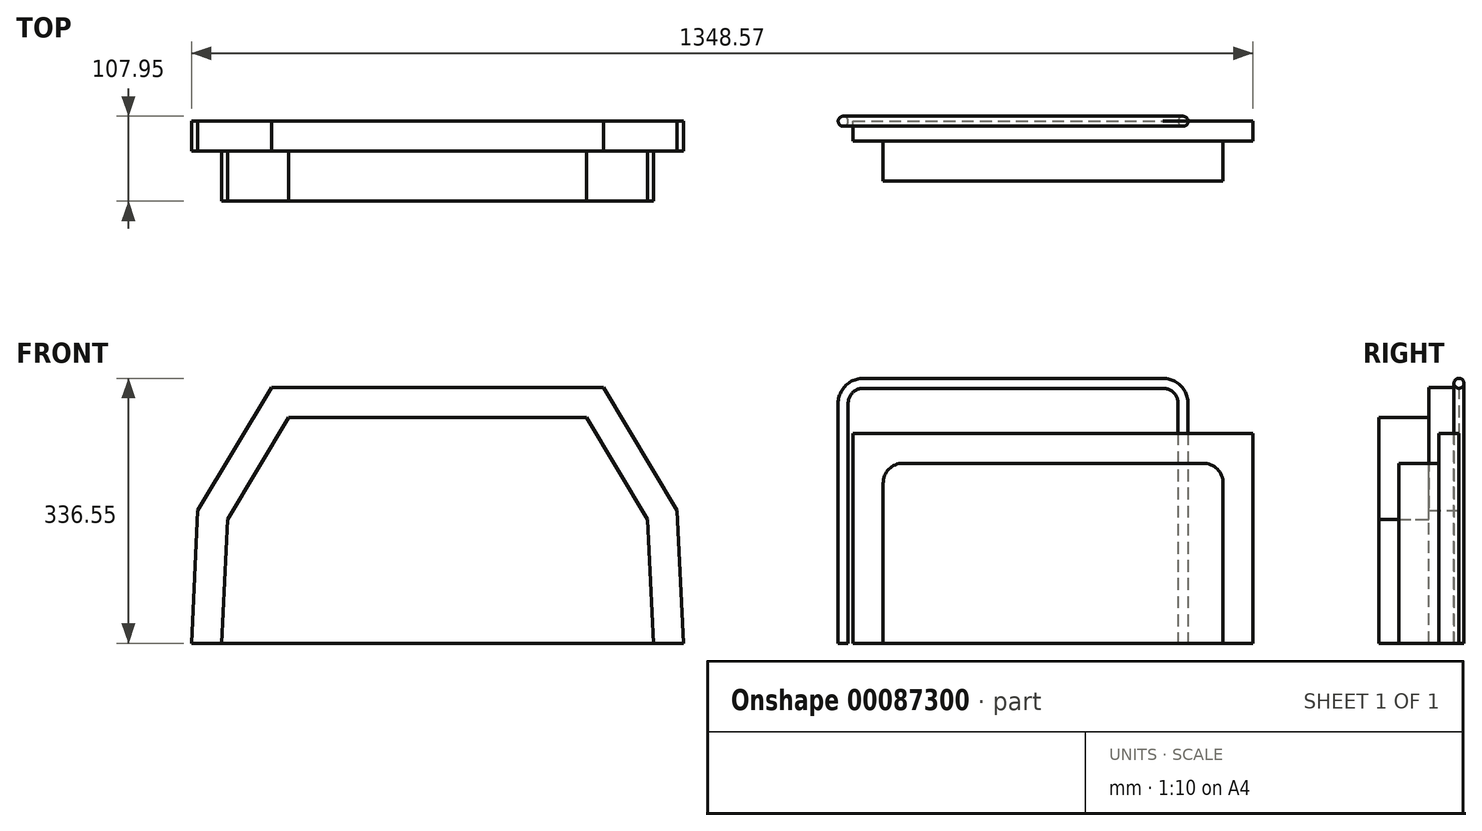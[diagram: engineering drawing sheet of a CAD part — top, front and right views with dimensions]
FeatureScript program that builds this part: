
annotation { "Feature Type Name" : "Feature", "Feature Type Description" : "" }
export const myFeature = defineFeature(function(context is Context, id is Id, definition is map)
    precondition{}
    {
        {
            var Q0;
            Q0=qCreatedBy(makeId("Front.planeOp"),FACE);
            var sketch = newSketch(context, id + "F0", { "sketchPlane" : qUnion([Q0])});
            skLineSegment(sketch, "E0", {"start": v(-274.32, 0) * mm, "end": v(0, 0) * mm});
            skLineSegment(sketch, "E1", {"start": v(274.32, 0) * mm, "end": v(266.7, 157.48) * mm});
            skLineSegment(sketch, "E2", {"start": v(266.7, 157.48) * mm, "end": v(189.23, 287.02) * mm});
            skLineSegment(sketch, "E3", {"start": v(189.23, 287.02) * mm, "end": v(-189.23, 287.02) * mm});
            skLineSegment(sketch, "E4", {"start": v(-189.23, 287.02) * mm, "end": v(-266.7, 157.48) * mm});
            skLineSegment(sketch, "E5", {"start": v(-266.7, 157.48) * mm, "end": v(-274.32, 0) * mm});
            skLineSegment(sketch, "E6", {"start": v(-266.7, 157.48) * mm, "end": v(-189.23, 157.48) * mm, "construction": true});
            skLineSegment(sketch, "E7", {"start": v(0, 157.48) * mm, "end": v(189.23, 157.48) * mm, "construction": true});
            skLineSegment(sketch, "E8", {"start": v(0, 157.48) * mm, "end": v(0, 0) * mm, "construction": true});
            skLineSegment(sketch, "E9", {"start": v(-189.23, 287.02) * mm, "end": v(-189.23, 157.48) * mm, "construction": true});
            skLineSegment(sketch, "E10", {"start": v(189.23, 287.02) * mm, "end": v(189.23, 157.48) * mm, "construction": true});
            skLineSegment(sketch, "E11", {"start": v(-189.23, 157.48) * mm, "end": v(0, 157.48) * mm, "construction": true});
            skLineSegment(sketch, "E12", {"start": v(189.23, 157.48) * mm, "end": v(189.23, 157.48) * mm});
            skLineSegment(sketch, "E13", {"start": v(189.23, 157.48) * mm, "end": v(266.7, 157.48) * mm, "construction": true});
            skLineSegment(sketch, "E14", {"start": v(0, 0) * mm, "end": v(274.32, 0) * mm});
            skLineSegment(sketch, "E15", {"start": v(0, 287.02) * mm, "end": v(0, 157.48) * mm, "construction": true});
            skLineSegment(sketch, "E16.0", {"start": v(-304.3, 168.85) * mm, "end": v(-312.46, 0) * mm});
            skLineSegment(sketch, "E16.1", {"start": v(312.46, 0) * mm, "end": v(304.3, 168.85) * mm});
            skLineSegment(sketch, "E16.2", {"start": v(304.3, 168.85) * mm, "end": v(210.84, 325.12) * mm});
            skLineSegment(sketch, "E16.3", {"start": v(210.84, 325.12) * mm, "end": v(-210.84, 325.12) * mm});
            skLineSegment(sketch, "E16.4", {"start": v(-210.84, 325.12) * mm, "end": v(-304.3, 168.85) * mm});
            skLineSegment(sketch, "E17", {"start": v(-274.32, 0) * mm, "end": v(-312.46, 0) * mm});
            skLineSegment(sketch, "E18", {"start": v(274.32, 0) * mm, "end": v(312.46, 0) * mm});
            skLineSegment(sketch, "E19.bottom", {"start": v(566.21, 0) * mm, "end": v(998.01, 0) * mm});
            skLineSegment(sketch, "E19.top", {"start": v(591.61, 228.6) * mm, "end": v(972.61, 228.6) * mm});
            skLineSegment(sketch, "E19.left", {"start": v(566.21, 0) * mm, "end": v(566.21, 203.2) * mm});
            skLineSegment(sketch, "E19.right", {"start": v(998.01, 0) * mm, "end": v(998.01, 203.2) * mm});
            skPoint(sketch, "E20.visualSharp", {"position": v(566.21, 228.6) * mm});
            skArc(sketch, "E20.filletArc", {"start": v(591.61, 228.6) * mm, "mid": v(573.65, 221.16) * mm, "end": v(566.21, 203.2) * mm});
            skPoint(sketch, "E21.visualSharp", {"position": v(998.01, 228.6) * mm});
            skArc(sketch, "E21.filletArc", {"start": v(998.01, 203.2) * mm, "mid": v(990.57, 221.16) * mm, "end": v(972.61, 228.6) * mm});
            skLineSegment(sketch, "E22.bottom", {"start": v(528.11, 0) * mm, "end": v(1036.11, 0) * mm});
            skLineSegment(sketch, "E22.top", {"start": v(528.11, 266.7) * mm, "end": v(1036.11, 266.7) * mm});
            skLineSegment(sketch, "E22.left", {"start": v(528.11, 0) * mm, "end": v(528.11, 266.7) * mm});
            skLineSegment(sketch, "E22.right", {"start": v(1036.11, 0) * mm, "end": v(1036.11, 266.7) * mm});
            skLineSegment(sketch, "E23", {"start": v(782.11, 266.7) * mm, "end": v(782.11, 228.6) * mm, "construction": true});
            skLineSegment(sketch, "E24", {"start": v(566.21, 101.6) * mm, "end": v(528.11, 101.6) * mm, "construction": true});
            skLineSegment(sketch, "E25", {"start": v(998.01, 101.6) * mm, "end": v(1036.11, 101.6) * mm, "construction": true});
            skSolve(sketch);
        }
        {
            var Q0;
            Q0=makeQuery(id+"F0.imprint","IMPRINT",FACE,{"disambiguationData":[TD([[makeQuery(id+"F0.imprint","IMPRINT",EDGE,{"derivedFrom":sQuery(id+"F0.wireOp",EDGE,"E0")}),1.0]])]});
            extrude(context, id + "F1", {"entities" : qUnion([Q0]), "depth" : 101.6 * mm});
        }
        {
            var Q0;
            Q0=makeQuery(id+"F0.imprint","IMPRINT",FACE,{"disambiguationData":[TD([[makeQuery(id+"F0.imprint","IMPRINT",EDGE,{"derivedFrom":sQuery(id+"F0.wireOp",EDGE,"E1")}),-1.0]])]});
            extrude(context, id + "F2", {"entities" : qUnion([Q0]), "operationType" : NewBodyOperationType.ADD, "depth" : 38.1 * mm});
        }
        {
            var Q0;
            Q0=makeQuery(id+"F0.imprint","IMPRINT",FACE,{"disambiguationData":[TD([[makeQuery(id+"F0.imprint","IMPRINT",EDGE,{"derivedFrom":sQuery(id+"F0.wireOp",EDGE,"E19.top")}),1.0]])]});
            extrude(context, id + "F3", {"entities" : qUnion([Q0]), "depth" : 25.4 * mm});
        }
        {
            var Q0;
            Q0=makeQuery(id+"F0.imprint","IMPRINT",FACE,{"disambiguationData":[TD([[makeQuery(id+"F0.imprint","IMPRINT",EDGE,{"derivedFrom":sQuery(id+"F0.wireOp",EDGE,"E19.bottom")}),1.0]])]});
            extrude(context, id + "F4", {"entities" : qUnion([Q0]), "operationType" : NewBodyOperationType.ADD, "depth" : 76.2 * mm});
        }
        {
            var Q0;
            {var subQ0=sQuery(id+"F0.wireOp",EDGE,"E21.filletArc");var subQ1=sQuery(id+"F0.wireOp",EDGE,"E20.filletArc");var subQ2=sQuery(id+"F0.wireOp",EDGE,"E19.right");var subQ3=sQuery(id+"F0.wireOp",EDGE,"E19.left");var subQ4=sQuery(id+"F0.wireOp",EDGE,"E19.top");Q0=makeQuery(id+"F4.boolean.opBoolean","MERGE",FACE,{"derivedFrom":[makeQuery(id+"F3.opExtrude","CAP_FACE",FACE,{"disambiguationData":[OSD([subQ4,subQ3,subQ2,subQ1,subQ0,sQuery(id+"F0.wireOp",EDGE,"E22.bottom"),sQuery(id+"F0.wireOp",EDGE,"E22.top"),sQuery(id+"F0.wireOp",EDGE,"E22.left"),sQuery(id+"F0.wireOp",EDGE,"E22.right")])],"isStart":true}),makeQuery(id+"F4.opExtrude","CAP_FACE",FACE,{"disambiguationData":[OSD([sQuery(id+"F0.wireOp",EDGE,"E19.bottom"),subQ4,subQ3,subQ2,subQ1,subQ0])],"isStart":true})]});}
            var sketch = newSketch(context, id + "F5", { "sketchPlane" : qUnion([Q0])});
            skLineSegment(sketch, "E26", {"start": v(-515.41, 101.6) * mm, "end": v(-515.41, 0) * mm});
            skLineSegment(sketch, "E27", {"start": v(-515.41, 101.6) * mm, "end": v(-515.41, 304.8) * mm});
            skLineSegment(sketch, "E28", {"start": v(-540.81, 330.2) * mm, "end": v(-921.81, 330.2) * mm});
            skLineSegment(sketch, "E29", {"start": v(-947.21, 304.8) * mm, "end": v(-947.21, 101.6) * mm});
            skLineSegment(sketch, "E30", {"start": v(-947.21, 101.6) * mm, "end": v(-947.21, 0) * mm});
            skPoint(sketch, "E31.visualSharp", {"position": v(-947.21, 330.2) * mm});
            skArc(sketch, "E31.filletArc", {"start": v(-921.81, 330.2) * mm, "mid": v(-939.77, 322.76) * mm, "end": v(-947.21, 304.8) * mm});
            skPoint(sketch, "E32.visualSharp", {"position": v(-515.41, 330.2) * mm});
            skArc(sketch, "E32.filletArc", {"start": v(-515.41, 304.8) * mm, "mid": v(-522.85, 322.76) * mm, "end": v(-540.81, 330.2) * mm});
            skSolve(sketch);
        }
        {
            var Q0;
            Q0=qCreatedBy(makeId("Top.planeOp"),FACE);
            var sketch = newSketch(context, id + "F6", { "sketchPlane" : qUnion([Q0])});
            skPoint(sketch, "E33.0", {"position": v(515.41, 0) * mm});
            skCircle(sketch, "E34", {"center": v(515.41, 0) * mm, "radius": 6.35 * mm});
            skSolve(sketch);
        }
        {
            var Q0;
            Q0 = qSketchRegion(id + "F6", true);
            var Q1;
            Q1 = qConstructionFilter(qBodyType(qCreatedBy(id + "F5" ,EDGE), BodyType.WIRE), ConstructionObject.NO);
            sweep(context, id + "F7", {"profiles" : qUnion([Q0]), "path" : qUnion([Q1])});
        }
    });
